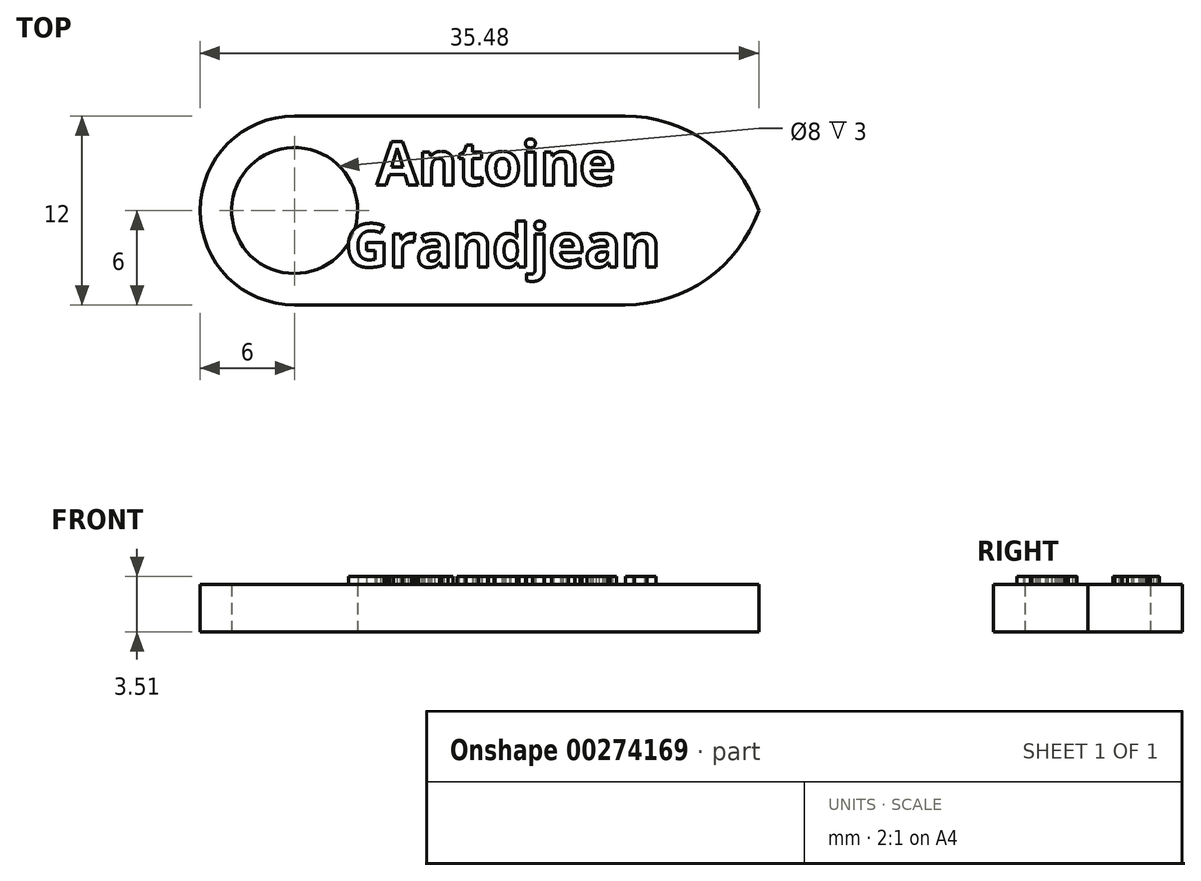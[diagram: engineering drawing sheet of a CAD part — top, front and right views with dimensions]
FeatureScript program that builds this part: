
annotation { "Feature Type Name" : "Feature", "Feature Type Description" : "" }
export const myFeature = defineFeature(function(context is Context, id is Id, definition is map)
    precondition{}
    {
        {
            var Q0;
            Q0=qCreatedBy(makeId("Top.planeOp"),FACE);
            var sketch = newSketch(context, id + "F0", { "sketchPlane" : qUnion([Q0])});
            skLineSegment(sketch, "E0.bottom", {"start": v(0, 0) * mm, "end": v(30, 0) * mm});
            skLineSegment(sketch, "E0.top", {"start": v(0, 12) * mm, "end": v(30, 12) * mm});
            skLineSegment(sketch, "E0.left", {"start": v(0, 0) * mm, "end": v(0, 12) * mm});
            skLineSegment(sketch, "E0.right", {"start": v(30, 0) * mm, "end": v(30, 12) * mm});
            skArc(sketch, "E1", {"start": v(0, 12) * mm, "mid": v(-6, 6) * mm, "end": v(0, 0) * mm});
            skCircle(sketch, "E2", {"center": v(0, 6) * mm, "radius": 4 * mm});
            skSolve(sketch);
        }
        {
            var Q0;
            {var subQ0=sQuery(id+"F0.wireOp",EDGE,"E1");Q0=makeQuery(id+"F0.imprint","IMPRINT",FACE,{"disambiguationData":[TD([[makeQuery(id+"F0.imprint","IMPRINT",EDGE,{"derivedFrom":subQ0}),1.0]])]});}
            var Q1;
            {var subQ5=sQuery(id+"F0.wireOp",EDGE,"E0.bottom");Q1=makeQuery(id+"F0.imprint","IMPRINT",FACE,{"disambiguationData":[TD([[makeQuery(id+"F0.imprint","IMPRINT",EDGE,{"derivedFrom":subQ5}),1.0]])]});}
            var Q2;
            {var subQ0=sQuery(id+"F0.wireOp",EDGE,"E2");var subQ1=sQuery(id+"F0.wireOp",EDGE,"E0.left");var subQ2=makeQuery(id+"F0.imprint","INTERSECT",VERTEX,{"disambiguationData":[OD(0.0)],"derivedFrom":[subQ1,subQ0]});Q2=makeQuery(id+"F0.imprint","IMPRINT",FACE,{"disambiguationData":[TD([[makeQuery(id+"F0.imprint","IMPRINT",EDGE,{"disambiguationData":[TD([[subQ2,-1.0]])],"derivedFrom":subQ1}),-1.0]])]});}
            extrude(context, id + "F1", {"entities" : qUnion([Q0, Q1, Q2]), "depth" : 3 * mm});
        }
        {
            var Q0;
            Q0=makeQuery(id+"F1.opExtrude","CAP_FACE",FACE,{"disambiguationData":[OSD([sQuery(id+"F0.wireOp",EDGE,"E0.bottom"),sQuery(id+"F0.wireOp",EDGE,"E0.top"),sQuery(id+"F0.wireOp",EDGE,"E0.left"),sQuery(id+"F0.wireOp",EDGE,"E0.right"),sQuery(id+"F0.wireOp",EDGE,"E1"),sQuery(id+"F0.wireOp",EDGE,"E2")])],"isStart":false});
            var sketch = newSketch(context, id + "F2", { "sketchPlane" : qUnion([Q0])});
            skText(sketch, "E3", { "text": "  Antoine\nGrandjean", "fontName": "OpenSans-Bold.ttf"});
            const initialGuessF2  = {"E3": [0.0032, 0.00763, 1, 0, 0.00276]};
            skSetInitialGuess(sketch, initialGuessF2);
            skSolve(sketch);
        }
        {
            var Q0;
            Q0 = qSketchRegion(id + "F2", true);
            extrude(context, id + "F3", {"entities" : qUnion([Q0]), "operationType" : NewBodyOperationType.ADD, "depth" : 0.5 * mm});
        }
        {
            var Q0;
            Q0=makeQuery(id+"F1.opExtrude","SWEPT_EDGE",EDGE,{"disambiguationData":[OSD([sQuery(id+"F0.wireOp",EDGE,"E0.top"),sQuery(id+"F0.wireOp",EDGE,"E0.right")])]});
            var Q1;
            Q1=makeQuery(id+"F1.opExtrude","SWEPT_EDGE",EDGE,{"disambiguationData":[OSD([sQuery(id+"F0.wireOp",EDGE,"E0.bottom"),sQuery(id+"F0.wireOp",EDGE,"E0.right")])]});
            fillet(context, id + "F4", {"entities" : qUnion([Q0, Q1]), "radius" : 9 * mm, "tangentPropagation" : true, "allowEdgeOverflow" : false});
        }
    });
